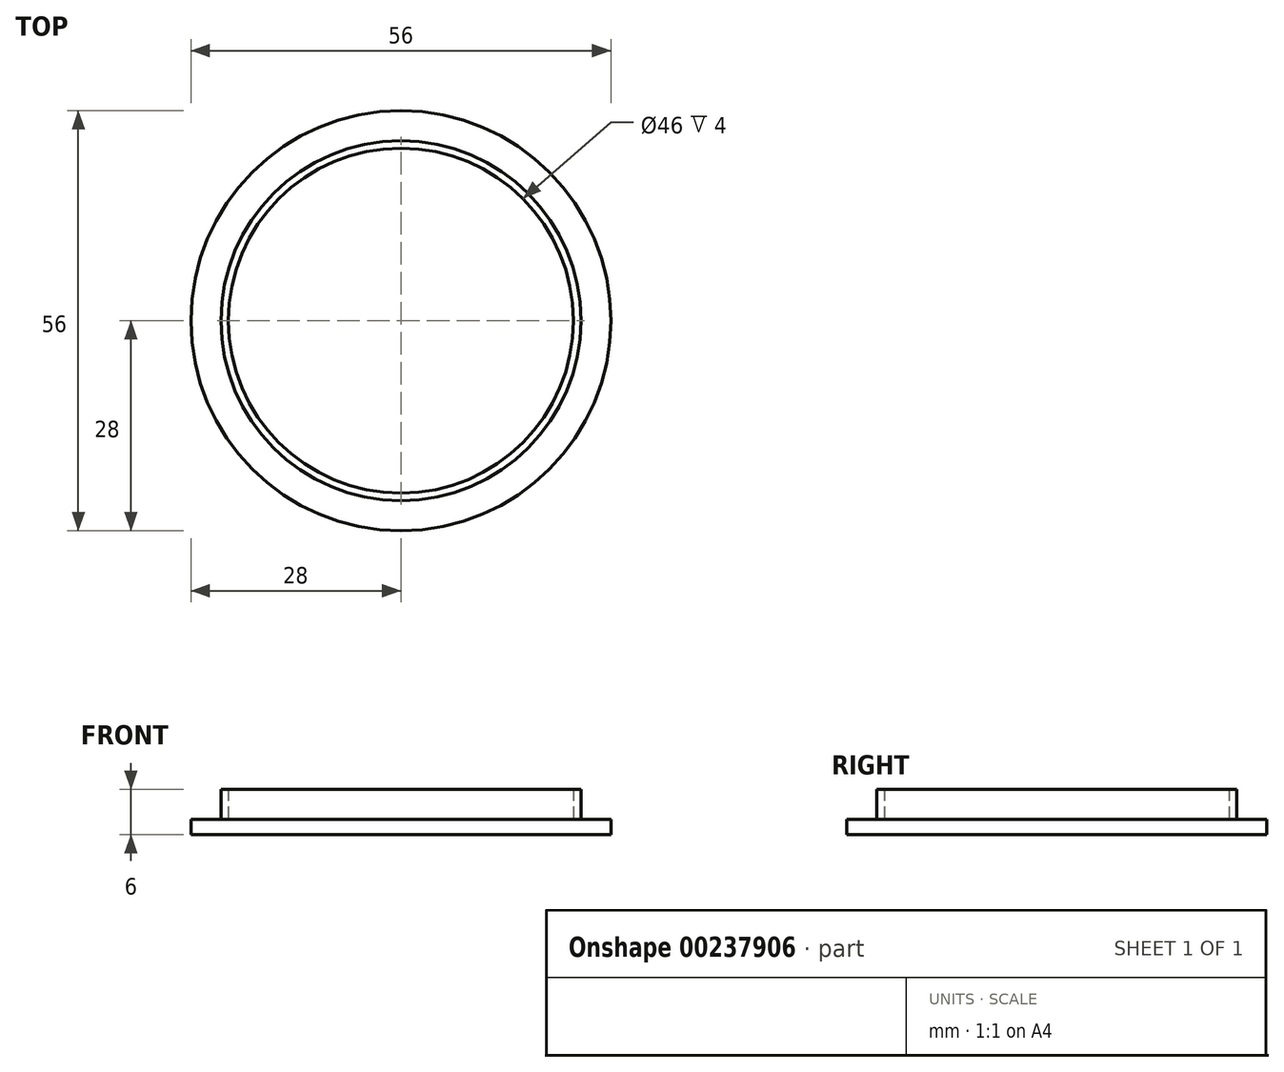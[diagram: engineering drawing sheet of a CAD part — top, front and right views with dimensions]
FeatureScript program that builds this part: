
annotation { "Feature Type Name" : "Feature", "Feature Type Description" : "" }
export const myFeature = defineFeature(function(context is Context, id is Id, definition is map)
    precondition{}
    {
        {
            var Q0;
            Q0=qCreatedBy(makeId("Top.planeOp"),FACE);
            var sketch = newSketch(context, id + "F0", { "sketchPlane" : qUnion([Q0])});
            skCircle(sketch, "E0", {"center": v(0, 0) * mm, "radius": 24 * mm});
            skCircle(sketch, "E1", {"center": v(0, 0) * mm, "radius": 23 * mm});
            skCircle(sketch, "E2", {"center": v(0, 0) * mm, "radius": 28 * mm});
            skSolve(sketch);
        }
        {
            var Q0;
            Q0=makeQuery(id+"F0.imprint","IMPRINT",FACE,{"disambiguationData":[TD([[makeQuery(id+"F0.imprint","IMPRINT",EDGE,{"derivedFrom":sQuery(id+"F0.wireOp",EDGE,"E0")}),-1.0]])]});
            var Q1;
            Q1=makeQuery(id+"F0.imprint","IMPRINT",FACE,{"disambiguationData":[TD([[makeQuery(id+"F0.imprint","IMPRINT",EDGE,{"derivedFrom":sQuery(id+"F0.wireOp",EDGE,"E0")}),1.0]])]});
            var Q2;
            Q2=makeQuery(id+"F0.imprint","IMPRINT",FACE,{"disambiguationData":[TD([[makeQuery(id+"F0.imprint","IMPRINT",EDGE,{"derivedFrom":sQuery(id+"F0.wireOp",EDGE,"E1")}),1.0]])]});
            extrude(context, id + "F1", {"entities" : qUnion([Q0, Q1, Q2]), "oppositeDirection" : true, "depth" : 2 * mm, "offsetDistance" : 25 * mm});
        }
        {
            var Q0;
            Q0=makeQuery(id+"F0.imprint","IMPRINT",FACE,{"disambiguationData":[TD([[makeQuery(id+"F0.imprint","IMPRINT",EDGE,{"derivedFrom":sQuery(id+"F0.wireOp",EDGE,"E0")}),1.0]])]});
            extrude(context, id + "F2", {"entities" : qUnion([Q0]), "operationType" : NewBodyOperationType.ADD, "depth" : 4 * mm, "offsetDistance" : 25 * mm});
        }
    });
